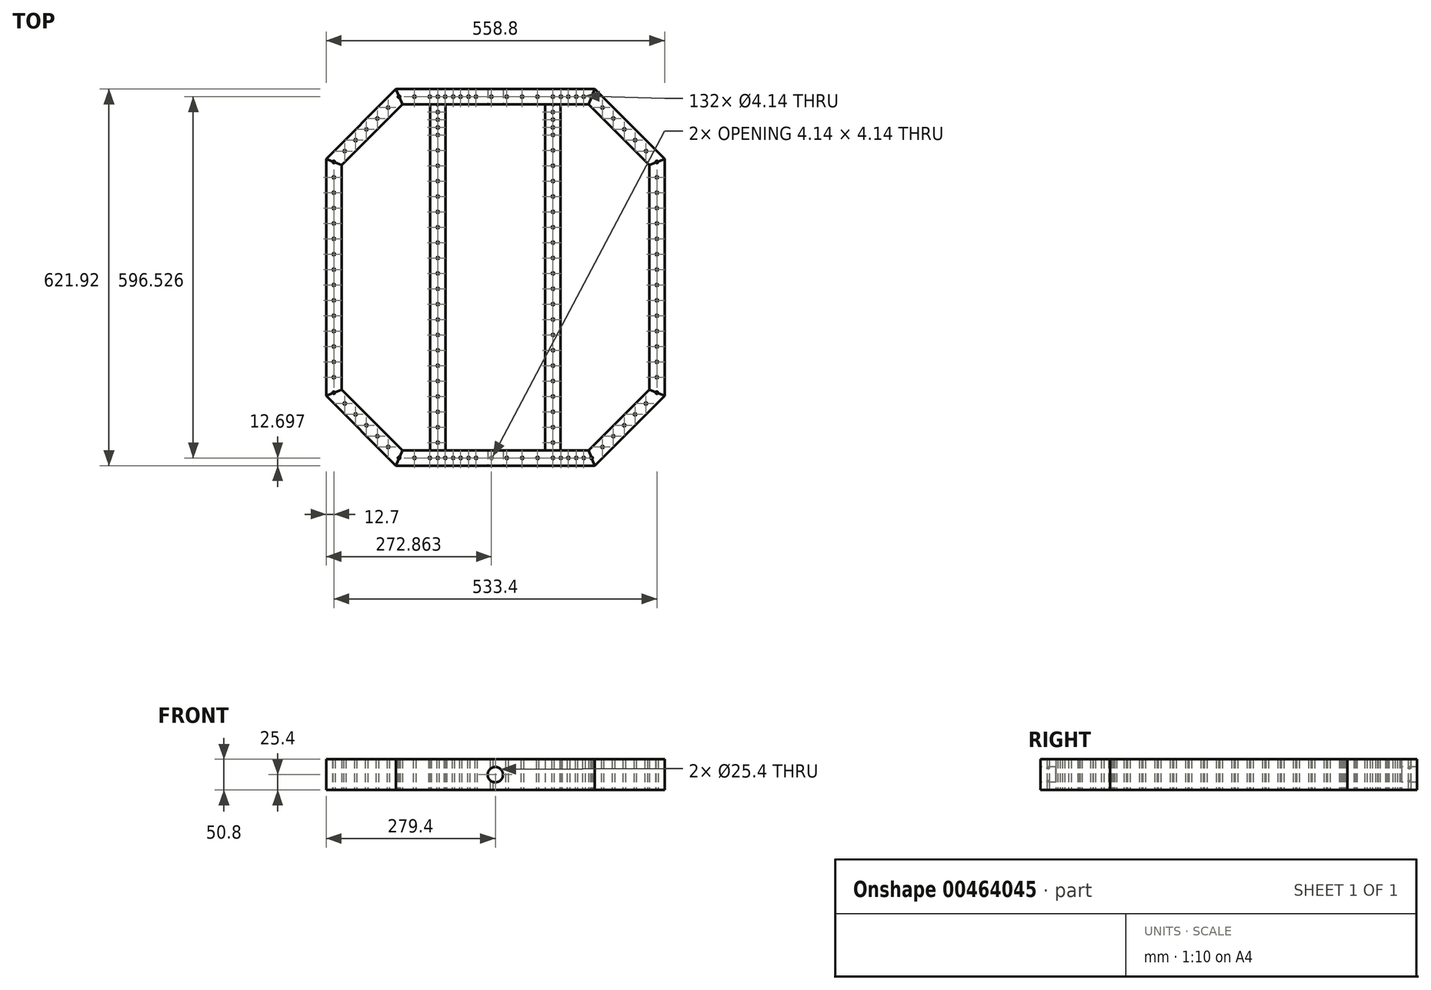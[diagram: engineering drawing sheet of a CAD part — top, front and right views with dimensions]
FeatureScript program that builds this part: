
annotation { "Feature Type Name" : "Feature", "Feature Type Description" : "" }
export const myFeature = defineFeature(function(context is Context, id is Id, definition is map)
    precondition{}
    {
        {
            var Q0;
            Q0=qCreatedBy(makeId("Top.planeOp"),FACE);
            var sketch = newSketch(context, id + "F0", { "sketchPlane" : qUnion([Q0])});
            skLineSegment(sketch, "E0.MirrorCS", {"start": v(-266.7, -185.24) * mm, "end": v(-277.49, -189.7) * mm});
            skLineSegment(sketch, "E1.MirrorCS", {"start": v(-292.1, -195.76) * mm, "end": v(-176.9, -310.96) * mm});
            skCircle(sketch, "E2.0.8.0", {"center": v(-279.4, -12.7) * mm, "radius": 2.07 * mm});
            skCircle(sketch, "E2.0.9.0", {"center": v(-279.4, -38.1) * mm, "radius": 2.07 * mm});
            skCircle(sketch, "E2.0.10.0", {"center": v(-279.4, -63.5) * mm, "radius": 2.07 * mm});
            skCircle(sketch, "E2.0.11.0", {"center": v(-279.4, -88.9) * mm, "radius": 2.07 * mm});
            skCircle(sketch, "E2.0.12.0", {"center": v(-279.4, -114.3) * mm, "radius": 2.07 * mm});
            skCircle(sketch, "E2.0.13.0", {"center": v(-279.4, -139.7) * mm, "radius": 2.07 * mm});
            skCircle(sketch, "E2.0.14.0", {"center": v(-279.4, -165.1) * mm, "radius": 2.07 * mm});
            skCircle(sketch, "E2.0.15.0", {"center": v(-279.4, -190.5) * mm, "radius": 2.07 * mm});
            skCircle(sketch, "E3.MirrorC", {"center": v(-171.64, -298.26) * mm, "radius": 2.07 * mm});
            skLineSegment(sketch, "E4.MirrorCS", {"start": v(-166.38, -285.56) * mm, "end": v(-170.84, -296.35) * mm});
            skCircle(sketch, "E5.MirrorC", {"center": v(-146.24, -298.26) * mm, "radius": 2.07 * mm});
            skCircle(sketch, "E6.MirrorC", {"center": v(-207.56, -262.34) * mm, "radius": 2.07 * mm});
            skCircle(sketch, "E7.MirrorC", {"center": v(-225.52, -244.38) * mm, "radius": 2.07 * mm});
            skCircle(sketch, "E8.MirrorC", {"center": v(-95.44, -298.26) * mm, "radius": 2.07 * mm});
            skCircle(sketch, "E9.MirrorC", {"center": v(-120.84, -298.26) * mm, "radius": 2.07 * mm});
            skCircle(sketch, "E10.MirrorC", {"center": v(-189.6, -280.3) * mm, "radius": 2.07 * mm});
            skCircle(sketch, "E11.MirrorC", {"center": v(-19.24, -298.26) * mm, "radius": 2.07 * mm});
            skCircle(sketch, "E12.MirrorC", {"center": v(-261.44, -208.46) * mm, "radius": 2.07 * mm});
            skCircle(sketch, "E13.MirrorC", {"center": v(-44.64, -298.26) * mm, "radius": 2.07 * mm});
            skCircle(sketch, "E14.MirrorC", {"center": v(-70.04, -298.26) * mm, "radius": 2.07 * mm});
            skCircle(sketch, "E15.MirrorC", {"center": v(-243.48, -226.42) * mm, "radius": 2.07 * mm});
            skCircle(sketch, "E16.MirrorC", {"center": v(254, -190.5) * mm, "radius": 2.07 * mm});
            skLineSegment(sketch, "E17.MirrorCS", {"start": v(241.3, -185.24) * mm, "end": v(252.09, -189.7) * mm});
            skCircle(sketch, "E18.MirrorC", {"center": v(236.04, -208.46) * mm, "radius": 2.07 * mm});
            skCircle(sketch, "E19.MirrorC", {"center": v(146.24, -298.26) * mm, "radius": 2.07 * mm});
            skLineSegment(sketch, "E20.MirrorCS", {"start": v(140.98, -285.56) * mm, "end": v(145.44, -296.35) * mm});
            skCircle(sketch, "E21.MirrorC", {"center": v(254, -165.1) * mm, "radius": 2.07 * mm});
            skCircle(sketch, "E22.MirrorC", {"center": v(120.84, -298.26) * mm, "radius": 2.07 * mm});
            skCircle(sketch, "E23.MirrorC", {"center": v(254, -139.7) * mm, "radius": 2.07 * mm});
            skCircle(sketch, "E24.MirrorC", {"center": v(254, -12.7) * mm, "radius": 2.07 * mm});
            skCircle(sketch, "E25.MirrorC", {"center": v(218.08, -226.42) * mm, "radius": 2.07 * mm});
            skCircle(sketch, "E26.MirrorC", {"center": v(200.12, -244.38) * mm, "radius": 2.07 * mm});
            skLineSegment(sketch, "E27.MirrorCS", {"start": v(266.7, -195.76) * mm, "end": v(151.5, -310.96) * mm});
            skCircle(sketch, "E28.MirrorC", {"center": v(254, -88.9) * mm, "radius": 2.07 * mm});
            skCircle(sketch, "E29.MirrorC", {"center": v(164.2, -280.3) * mm, "radius": 2.07 * mm});
            skCircle(sketch, "E30.MirrorC", {"center": v(254, -38.1) * mm, "radius": 2.07 * mm});
            skCircle(sketch, "E31.MirrorC", {"center": v(254, -63.5) * mm, "radius": 2.07 * mm});
            skCircle(sketch, "E32.MirrorC", {"center": v(254, -114.3) * mm, "radius": 2.07 * mm});
            skCircle(sketch, "E33.MirrorC", {"center": v(95.44, -298.26) * mm, "radius": 2.07 * mm});
            skCircle(sketch, "E34.MirrorC", {"center": v(182.16, -262.34) * mm, "radius": 2.07 * mm});
            skCircle(sketch, "E35.1.0.0", {"center": v(6.16, -298.26) * mm, "radius": 2.07 * mm});
            skCircle(sketch, "E35.2.0.0", {"center": v(31.56, -298.26) * mm, "radius": 2.07 * mm});
            skCircle(sketch, "E35.3.0.0", {"center": v(56.96, -298.26) * mm, "radius": 2.07 * mm});
            skCircle(sketch, "E35.4.0.0", {"center": v(82.36, -298.26) * mm, "radius": 2.07 * mm});
            skCircle(sketch, "E35.5.0.0", {"center": v(107.76, -298.26) * mm, "radius": 2.07 * mm});
            skCircle(sketch, "E35.6.0.0", {"center": v(133.16, -298.26) * mm, "radius": 2.07 * mm});
            skLineSegment(sketch, "E36", {"start": v(-166.38, -285.56) * mm, "end": v(-266.7, -185.24) * mm});
            skLineSegment(sketch, "E37", {"start": v(-166.38, -285.56) * mm, "end": v(140.98, -285.56) * mm});
            skLineSegment(sketch, "E38", {"start": v(241.3, -185.24) * mm, "end": v(140.98, -285.56) * mm});
            skLineSegment(sketch, "E39", {"start": v(69.66, -285.56) * mm, "end": v(69.66, 0) * mm});
            skLineSegment(sketch, "E40", {"start": v(95.06, -285.56) * mm, "end": v(95.06, 0) * mm});
            skPoint(sketch, "E41.orphan", {"position": v(69.66, -298.26) * mm});
            skPoint(sketch, "E42.orphan", {"position": v(95.06, -298.26) * mm});
            skLineSegment(sketch, "E43.MirrorCS", {"start": v(-95.06, -285.56) * mm, "end": v(-95.06, 0) * mm});
            skLineSegment(sketch, "E44.MirrorCS", {"start": v(-120.46, -285.56) * mm, "end": v(-120.46, 0) * mm});
            skPoint(sketch, "E45.start.orphan", {"position": v(-12.7, -310.96) * mm});
            skLineSegment(sketch, "E46.trimOffspring", {"start": v(255.91, -191.3) * mm, "end": v(266.7, -195.76) * mm});
            skLineSegment(sketch, "E47.trimOffspring", {"start": v(147.03, -300.18) * mm, "end": v(151.5, -310.96) * mm});
            skLineSegment(sketch, "E48.trimOffspring", {"start": v(-281.31, -191.3) * mm, "end": v(-292.1, -195.76) * mm});
            skLineSegment(sketch, "E49.trimOffspring", {"start": v(-172.43, -300.18) * mm, "end": v(-176.9, -310.96) * mm});
            skCircle(sketch, "E50.MirrorC", {"center": v(-279.4, 190.5) * mm, "radius": 2.07 * mm});
            skLineSegment(sketch, "E51.MirrorCS", {"start": v(-281.31, 191.3) * mm, "end": v(-292.1, 195.76) * mm});
            skLineSegment(sketch, "E52.MirrorCS", {"start": v(255.91, 191.3) * mm, "end": v(266.7, 195.76) * mm});
            skLineSegment(sketch, "E53.MirrorCS", {"start": v(-172.43, 300.18) * mm, "end": v(-176.9, 310.96) * mm});
            skCircle(sketch, "E54.MirrorC", {"center": v(-171.64, 298.26) * mm, "radius": 2.07 * mm});
            skCircle(sketch, "E55.MirrorC", {"center": v(146.24, 298.26) * mm, "radius": 2.07 * mm});
            skLineSegment(sketch, "E56.MirrorCS", {"start": v(-266.7, 185.24) * mm, "end": v(-277.49, 189.7) * mm});
            skCircle(sketch, "E57.MirrorC", {"center": v(254, 190.5) * mm, "radius": 2.07 * mm});
            skLineSegment(sketch, "E58.MirrorCS", {"start": v(147.03, 300.18) * mm, "end": v(151.5, 310.96) * mm});
            skLineSegment(sketch, "E59.MirrorCS", {"start": v(-166.38, 285.56) * mm, "end": v(-170.84, 296.35) * mm});
            skCircle(sketch, "E60.MirrorC", {"center": v(254, 139.7) * mm, "radius": 2.07 * mm});
            skLineSegment(sketch, "E61.MirrorCS", {"start": v(241.3, 185.24) * mm, "end": v(252.09, 189.7) * mm});
            skCircle(sketch, "E62.MirrorC", {"center": v(133.16, 298.26) * mm, "radius": 2.07 * mm});
            skCircle(sketch, "E63.MirrorC", {"center": v(-279.4, 139.7) * mm, "radius": 2.07 * mm});
            skLineSegment(sketch, "E64.MirrorCS", {"start": v(140.98, 285.56) * mm, "end": v(145.44, 296.35) * mm});
            skCircle(sketch, "E65.MirrorC", {"center": v(-279.4, 165.1) * mm, "radius": 2.07 * mm});
            skCircle(sketch, "E66.MirrorC", {"center": v(254, 165.1) * mm, "radius": 2.07 * mm});
            skCircle(sketch, "E67.MirrorC", {"center": v(-120.84, 298.26) * mm, "radius": 2.07 * mm});
            skCircle(sketch, "E68.MirrorC", {"center": v(-279.4, 12.7) * mm, "radius": 2.07 * mm});
            skCircle(sketch, "E69.MirrorC", {"center": v(82.36, 298.26) * mm, "radius": 2.07 * mm});
            skCircle(sketch, "E70.MirrorC", {"center": v(-19.24, 298.26) * mm, "radius": 2.07 * mm});
            skCircle(sketch, "E71.MirrorC", {"center": v(6.16, 298.26) * mm, "radius": 2.07 * mm});
            skCircle(sketch, "E72.MirrorC", {"center": v(107.76, 298.26) * mm, "radius": 2.07 * mm});
            skCircle(sketch, "E73.MirrorC", {"center": v(95.44, 298.26) * mm, "radius": 2.07 * mm});
            skCircle(sketch, "E74.MirrorC", {"center": v(120.84, 298.26) * mm, "radius": 2.07 * mm});
            skCircle(sketch, "E75.MirrorC", {"center": v(-189.6, 280.3) * mm, "radius": 2.07 * mm});
            skCircle(sketch, "E76.MirrorC", {"center": v(-279.4, 88.9) * mm, "radius": 2.07 * mm});
            skCircle(sketch, "E77.MirrorC", {"center": v(-261.44, 208.46) * mm, "radius": 2.07 * mm});
            skCircle(sketch, "E78.MirrorC", {"center": v(-279.4, 114.3) * mm, "radius": 2.07 * mm});
            skCircle(sketch, "E79.MirrorC", {"center": v(200.12, 244.38) * mm, "radius": 2.07 * mm});
            skCircle(sketch, "E80.MirrorC", {"center": v(-279.4, 38.1) * mm, "radius": 2.07 * mm});
            skCircle(sketch, "E81.MirrorC", {"center": v(254, 38.1) * mm, "radius": 2.07 * mm});
            skCircle(sketch, "E82.MirrorC", {"center": v(218.08, 226.42) * mm, "radius": 2.07 * mm});
            skCircle(sketch, "E83.MirrorC", {"center": v(-279.4, 63.5) * mm, "radius": 2.07 * mm});
            skCircle(sketch, "E84.MirrorC", {"center": v(-95.44, 298.26) * mm, "radius": 2.07 * mm});
            skCircle(sketch, "E85.MirrorC", {"center": v(164.2, 280.3) * mm, "radius": 2.07 * mm});
            skCircle(sketch, "E86.MirrorC", {"center": v(254, 12.7) * mm, "radius": 2.07 * mm});
            skCircle(sketch, "E87.MirrorC", {"center": v(56.96, 298.26) * mm, "radius": 2.07 * mm});
            skCircle(sketch, "E88.MirrorC", {"center": v(254, 88.9) * mm, "radius": 2.07 * mm});
            skCircle(sketch, "E89.MirrorC", {"center": v(-70.04, 298.26) * mm, "radius": 2.07 * mm});
            skCircle(sketch, "E90.MirrorC", {"center": v(-243.48, 226.42) * mm, "radius": 2.07 * mm});
            skCircle(sketch, "E91.MirrorC", {"center": v(236.04, 208.46) * mm, "radius": 2.07 * mm});
            skCircle(sketch, "E92.MirrorC", {"center": v(254, 63.5) * mm, "radius": 2.07 * mm});
            skLineSegment(sketch, "E93.MirrorCS", {"start": v(151.5, 310.96) * mm, "end": v(-176.9, 310.96) * mm});
            skCircle(sketch, "E94.MirrorC", {"center": v(-146.24, 298.26) * mm, "radius": 2.07 * mm});
            skCircle(sketch, "E95.MirrorC", {"center": v(-44.64, 298.26) * mm, "radius": 2.07 * mm});
            skCircle(sketch, "E96.MirrorC", {"center": v(-225.52, 244.38) * mm, "radius": 2.07 * mm});
            skCircle(sketch, "E97.MirrorC", {"center": v(254, 114.3) * mm, "radius": 2.07 * mm});
            skCircle(sketch, "E98.MirrorC", {"center": v(31.56, 298.26) * mm, "radius": 2.07 * mm});
            skLineSegment(sketch, "E99.MirrorCS", {"start": v(266.7, 195.76) * mm, "end": v(151.5, 310.96) * mm});
            skCircle(sketch, "E100.MirrorC", {"center": v(182.16, 262.34) * mm, "radius": 2.07 * mm});
            skLineSegment(sketch, "E101.MirrorCS", {"start": v(-292.1, 195.76) * mm, "end": v(-176.9, 310.96) * mm});
            skLineSegment(sketch, "E102.MirrorCS", {"start": v(-166.38, 285.56) * mm, "end": v(140.98, 285.56) * mm});
            skCircle(sketch, "E103.MirrorC", {"center": v(-207.56, 262.34) * mm, "radius": 2.07 * mm});
            skLineSegment(sketch, "E104.MirrorCS", {"start": v(95.06, 285.56) * mm, "end": v(95.06, 0) * mm});
            skLineSegment(sketch, "E105.MirrorCS", {"start": v(241.3, 185.24) * mm, "end": v(140.98, 285.56) * mm});
            skLineSegment(sketch, "E106.MirrorCS", {"start": v(-166.38, 285.56) * mm, "end": v(-266.7, 185.24) * mm});
            skLineSegment(sketch, "E107.MirrorCS", {"start": v(-120.46, 285.56) * mm, "end": v(-120.46, 0) * mm});
            skPoint(sketch, "E108.MirrorP", {"position": v(-12.7, 310.96) * mm});
            skPoint(sketch, "E109.MirrorP", {"position": v(69.66, 298.26) * mm});
            skLineSegment(sketch, "E110.MirrorCS", {"start": v(69.66, 285.56) * mm, "end": v(69.66, 0) * mm});
            skPoint(sketch, "E111.MirrorP", {"position": v(95.06, 298.26) * mm});
            skCircle(sketch, "E112.0.1.0", {"center": v(82.36, -272.86) * mm, "radius": 2.07 * mm});
            skCircle(sketch, "E112.0.2.0", {"center": v(82.36, -247.46) * mm, "radius": 2.07 * mm});
            skCircle(sketch, "E112.0.3.0", {"center": v(82.36, -222.06) * mm, "radius": 2.07 * mm});
            skCircle(sketch, "E112.0.4.0", {"center": v(82.36, -196.66) * mm, "radius": 2.07 * mm});
            skCircle(sketch, "E112.0.5.0", {"center": v(82.36, -171.26) * mm, "radius": 2.07 * mm});
            skCircle(sketch, "E112.0.6.0", {"center": v(82.36, -145.86) * mm, "radius": 2.07 * mm});
            skCircle(sketch, "E112.0.7.0", {"center": v(82.36, -120.46) * mm, "radius": 2.07 * mm});
            skCircle(sketch, "E112.0.8.0", {"center": v(82.36, -95.06) * mm, "radius": 2.07 * mm});
            skCircle(sketch, "E112.0.9.0", {"center": v(82.36, -69.66) * mm, "radius": 2.07 * mm});
            skCircle(sketch, "E112.0.10.0", {"center": v(82.36, -44.26) * mm, "radius": 2.07 * mm});
            skCircle(sketch, "E112.0.11.0", {"center": v(82.36, -18.86) * mm, "radius": 2.07 * mm});
            skCircle(sketch, "E112.0.12.0", {"center": v(82.36, 6.54) * mm, "radius": 2.07 * mm});
            skCircle(sketch, "E112.0.13.0", {"center": v(82.36, 31.94) * mm, "radius": 2.07 * mm});
            skCircle(sketch, "E112.0.14.0", {"center": v(82.36, 57.34) * mm, "radius": 2.07 * mm});
            skCircle(sketch, "E112.0.15.0", {"center": v(82.36, 82.74) * mm, "radius": 2.07 * mm});
            skCircle(sketch, "E112.0.16.0", {"center": v(82.36, 108.14) * mm, "radius": 2.07 * mm});
            skCircle(sketch, "E112.0.17.0", {"center": v(82.36, 133.54) * mm, "radius": 2.07 * mm});
            skCircle(sketch, "E112.0.18.0", {"center": v(82.36, 158.94) * mm, "radius": 2.07 * mm});
            skCircle(sketch, "E112.0.19.0", {"center": v(82.36, 184.34) * mm, "radius": 2.07 * mm});
            skCircle(sketch, "E112.0.20.0", {"center": v(82.36, 209.74) * mm, "radius": 2.07 * mm});
            skCircle(sketch, "E112.0.21.0", {"center": v(82.36, 235.14) * mm, "radius": 2.07 * mm});
            skCircle(sketch, "E112.0.22.0", {"center": v(82.36, 260.54) * mm, "radius": 2.07 * mm});
            skArc(sketch, "E112.0.23.0", {"start": v(84.4, 285.56) * mm, "mid": v(82.36, 283.87) * mm, "end": v(80.33, 285.56) * mm});
            skCircle(sketch, "E113.0.1.0", {"center": v(82.36, 272.86) * mm, "radius": 2.07 * mm});
            skCircle(sketch, "E113.0.2.0", {"center": v(82.36, 247.46) * mm, "radius": 2.07 * mm});
            skCircle(sketch, "E114.MirrorC", {"center": v(-107.76, 298.26) * mm, "radius": 2.07 * mm});
            skLineSegment(sketch, "E115.MirrorCS", {"start": v(-107.76, 298.26) * mm, "end": v(-107.76, 272.86) * mm, "construction": true});
            skArc(sketch, "E116.MirrorCS", {"start": v(-109.8, 285.56) * mm, "mid": v(-107.76, 283.87) * mm, "end": v(-105.73, 285.56) * mm});
            skCircle(sketch, "E117.MirrorC", {"center": v(-107.76, 272.86) * mm, "radius": 2.07 * mm});
            skCircle(sketch, "E118.MirrorC", {"center": v(-107.76, -298.26) * mm, "radius": 2.07 * mm});
            skCircle(sketch, "E119.MirrorC", {"center": v(-107.76, 260.54) * mm, "radius": 2.07 * mm});
            skLineSegment(sketch, "E120.MirrorCS", {"start": v(-107.76, -298.26) * mm, "end": v(-107.76, -272.86) * mm, "construction": true});
            skCircle(sketch, "E121.MirrorC", {"center": v(-107.76, -272.86) * mm, "radius": 2.07 * mm});
            skCircle(sketch, "E122.MirrorC", {"center": v(-82.36, 298.26) * mm, "radius": 2.07 * mm});
            skCircle(sketch, "E123.MirrorC", {"center": v(-107.76, 6.54) * mm, "radius": 2.07 * mm});
            skCircle(sketch, "E124.MirrorC", {"center": v(-107.76, 247.46) * mm, "radius": 2.07 * mm});
            skCircle(sketch, "E125.MirrorC", {"center": v(-82.36, -298.26) * mm, "radius": 2.07 * mm});
            skCircle(sketch, "E126.MirrorC", {"center": v(-107.76, -196.66) * mm, "radius": 2.07 * mm});
            skCircle(sketch, "E127.MirrorC", {"center": v(-107.76, 209.74) * mm, "radius": 2.07 * mm});
            skCircle(sketch, "E128.MirrorC", {"center": v(-107.76, 133.54) * mm, "radius": 2.07 * mm});
            skCircle(sketch, "E129.MirrorC", {"center": v(-107.76, 108.14) * mm, "radius": 2.07 * mm});
            skCircle(sketch, "E130.MirrorC", {"center": v(-107.76, -120.46) * mm, "radius": 2.07 * mm});
            skCircle(sketch, "E131.MirrorC", {"center": v(-107.76, -95.06) * mm, "radius": 2.07 * mm});
            skCircle(sketch, "E132.MirrorC", {"center": v(-107.76, -222.06) * mm, "radius": 2.07 * mm});
            skLineSegment(sketch, "E133.MirrorCS", {"start": v(-95.06, 285.56) * mm, "end": v(-95.06, 0) * mm});
            skCircle(sketch, "E134.MirrorC", {"center": v(-107.76, 158.94) * mm, "radius": 2.07 * mm});
            skCircle(sketch, "E135.MirrorC", {"center": v(-56.96, 298.26) * mm, "radius": 2.07 * mm});
            skCircle(sketch, "E136.MirrorC", {"center": v(-107.76, -247.46) * mm, "radius": 2.07 * mm});
            skCircle(sketch, "E137.MirrorC", {"center": v(-107.76, 82.74) * mm, "radius": 2.07 * mm});
            skCircle(sketch, "E138.MirrorC", {"center": v(-107.76, 235.14) * mm, "radius": 2.07 * mm});
            skCircle(sketch, "E139.MirrorC", {"center": v(-107.76, -171.26) * mm, "radius": 2.07 * mm});
            skCircle(sketch, "E140.MirrorC", {"center": v(-107.76, 57.34) * mm, "radius": 2.07 * mm});
            skCircle(sketch, "E141.MirrorC", {"center": v(-107.76, -145.86) * mm, "radius": 2.07 * mm});
            skCircle(sketch, "E142.MirrorC", {"center": v(-107.76, -69.66) * mm, "radius": 2.07 * mm});
            skCircle(sketch, "E143.MirrorC", {"center": v(-107.76, 31.94) * mm, "radius": 2.07 * mm});
            skCircle(sketch, "E144.MirrorC", {"center": v(-107.76, 184.34) * mm, "radius": 2.07 * mm});
            skCircle(sketch, "E145.MirrorC", {"center": v(-56.96, -298.26) * mm, "radius": 2.07 * mm});
            skLineSegment(sketch, "E146.MirrorCS", {"start": v(-176.9, -310.96) * mm, "end": v(151.5, -310.96) * mm});
            skCircle(sketch, "E147.MirrorC", {"center": v(-107.76, -18.86) * mm, "radius": 2.07 * mm});
            skCircle(sketch, "E148.MirrorC", {"center": v(-107.76, -44.26) * mm, "radius": 2.07 * mm});
            skPoint(sketch, "E149.MirrorP", {"position": v(-95.06, -298.26) * mm});
            skPoint(sketch, "E150.MirrorP", {"position": v(-95.06, 298.26) * mm});
            skLineSegment(sketch, "E151", {"start": v(-266.7, -185.24) * mm, "end": v(-266.7, 185.24) * mm});
            skLineSegment(sketch, "E152", {"start": v(-292.1, -195.76) * mm, "end": v(-292.1, 195.76) * mm});
            skLineSegment(sketch, "E153", {"start": v(266.7, -195.76) * mm, "end": v(266.7, 195.76) * mm});
            skLineSegment(sketch, "E154", {"start": v(241.3, -185.24) * mm, "end": v(241.3, 185.24) * mm});
            skSolve(sketch);
        }
        {
            var Q0;
            {var subQ1=sQuery(id+"F0.wireOp",EDGE,"E17.MirrorCS");Q0=makeQuery(id+"F0.imprint","IMPRINT",FACE,{"disambiguationData":[TD([[makeQuery(id+"F0.imprint","IMPRINT",EDGE,{"derivedFrom":subQ1}),1.0]])]});}
            var Q1;
            {var subQ2=sQuery(id+"F0.wireOp",EDGE,"E0.MirrorCS");Q1=makeQuery(id+"F0.imprint","IMPRINT",FACE,{"disambiguationData":[TD([[makeQuery(id+"F0.imprint","IMPRINT",EDGE,{"derivedFrom":subQ2}),-1.0]])]});}
            var Q2;
            {var subQ3=sQuery(id+"F0.wireOp",EDGE,"E4.MirrorCS");Q2=makeQuery(id+"F0.imprint","IMPRINT",FACE,{"disambiguationData":[TD([[makeQuery(id+"F0.imprint","IMPRINT",EDGE,{"derivedFrom":subQ3}),1.0]])]});}
            var Q3;
            {var subQ11=sQuery(id+"F0.wireOp",EDGE,"E53.MirrorCS");Q3=makeQuery(id+"F0.imprint","IMPRINT",FACE,{"disambiguationData":[TD([[makeQuery(id+"F0.imprint","IMPRINT",EDGE,{"derivedFrom":subQ11}),-1.0]])]});}
            extrude(context, id + "F1", {"entities" : qUnion([Q0, Q1, Q2, Q3]), "depth" : 50.8 * mm});
        }
        {
            var Q0;
            {var subQ3=sQuery(id+"F0.wireOp",EDGE,"E51.MirrorCS");Q0=makeQuery(id+"F0.imprint","IMPRINT",FACE,{"disambiguationData":[TD([[makeQuery(id+"F0.imprint","IMPRINT",EDGE,{"derivedFrom":subQ3}),-1.0]])]});}
            var Q1;
            {var subQ4=sQuery(id+"F0.wireOp",EDGE,"E52.MirrorCS");Q1=makeQuery(id+"F0.imprint","IMPRINT",FACE,{"disambiguationData":[TD([[makeQuery(id+"F0.imprint","IMPRINT",EDGE,{"derivedFrom":subQ4}),1.0]])]});}
            var Q2;
            {var subQ0=sQuery(id+"F0.wireOp",EDGE,"E39");Q2=makeQuery(id+"F0.imprint","IMPRINT",FACE,{"disambiguationData":[TD([[makeQuery(id+"F0.imprint","IMPRINT",EDGE,{"derivedFrom":subQ0}),-1.0]])]});}
            var Q3;
            {var subQ1=sQuery(id+"F0.wireOp",EDGE,"E17.MirrorCS");Q3=makeQuery(id+"F0.imprint","IMPRINT",FACE,{"disambiguationData":[TD([[makeQuery(id+"F0.imprint","IMPRINT",EDGE,{"derivedFrom":subQ1}),-1.0]])]});}
            var Q4;
            {var subQ0=sQuery(id+"F0.wireOp",EDGE,"E0.MirrorCS");Q4=makeQuery(id+"F0.imprint","IMPRINT",FACE,{"disambiguationData":[TD([[makeQuery(id+"F0.imprint","IMPRINT",EDGE,{"derivedFrom":subQ0}),1.0]])]});}
            var Q5;
            {var subQ4=sQuery(id+"F0.wireOp",EDGE,"E43.MirrorCS");Q5=makeQuery(id+"F0.imprint","IMPRINT",FACE,{"disambiguationData":[TD([[makeQuery(id+"F0.imprint","IMPRINT",EDGE,{"derivedFrom":subQ4}),1.0]])]});}
            extrude(context, id + "F2", {"entities" : qUnion([Q0, Q1, Q2, Q3, Q4, Q5]), "depth" : 50.8 * mm});
        }
        {
            var Q0;
            Q0=makeQuery(id+"F1.opExtrude","SWEPT_FACE",FACE,{"disambiguationData":[OSD([sQuery(id+"F0.wireOp",EDGE,"E146.MirrorCS")])]});
            var sketch = newSketch(context, id + "F3", { "sketchPlane" : qUnion([Q0])});
            skCircle(sketch, "E155", {"center": v(-12.7, 25.4) * mm, "radius": 12.7 * mm});
            skSolve(sketch);
        }
        {
            var Q0;
            Q0 = qSketchRegion(id + "F3", true);
            extrude(context, id + "F4", {"entities" : qUnion([Q0]), "operationType" : NewBodyOperationType.REMOVE, "endBound" : BoundingType.THROUGH_ALL, "oppositeDirection" : true, "depth" : 25.4 * mm});
        }
    });
